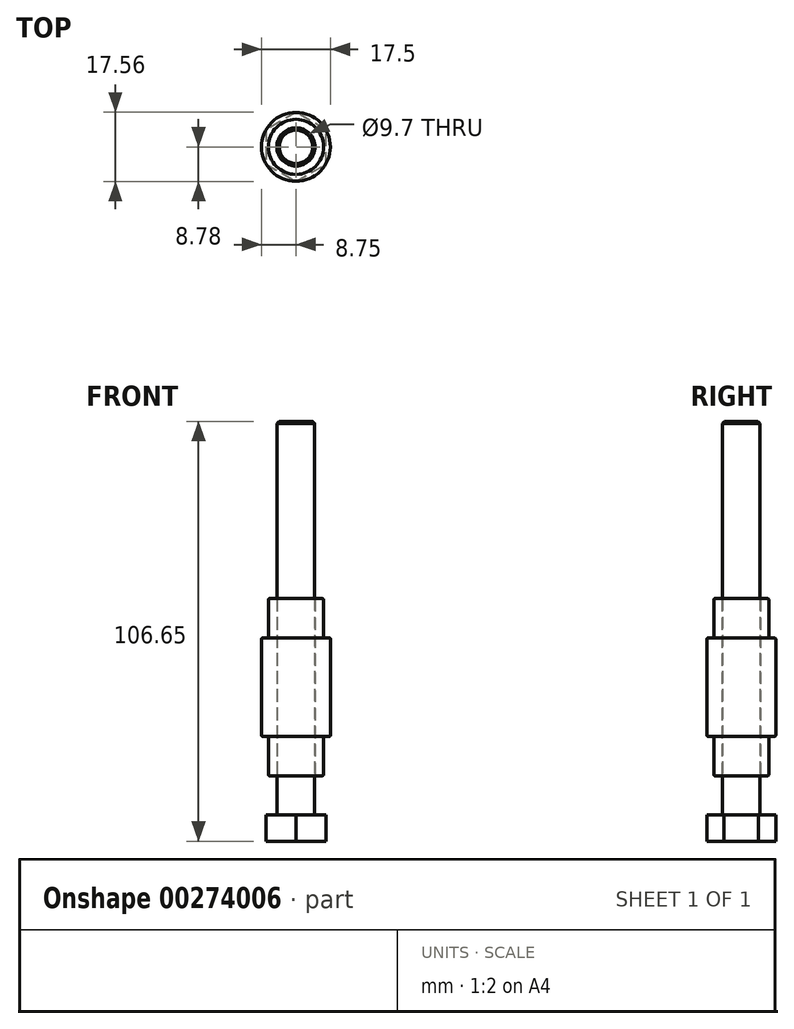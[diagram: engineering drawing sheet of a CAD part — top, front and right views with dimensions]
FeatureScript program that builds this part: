
annotation { "Feature Type Name" : "Feature", "Feature Type Description" : "" }
export const myFeature = defineFeature(function(context is Context, id is Id, definition is map)
    precondition{}
    {
        {
            var Q0;
            Q0=qCreatedBy(makeId("Top.planeOp"),FACE);
            var sketch = newSketch(context, id + "F0", { "sketchPlane" : qUnion([Q0])});
            skCircle(sketch, "E0", {"center": v(0, 0) * mm, "radius": 4.75 * mm});
            skSolve(sketch);
        }
        {
            var Q0;
            Q0=qSketchRegion(id+"F0",true);
            extrude(context, id + "F1", {"entities" : qUnion([Q0]), "depth" : 100 * mm});
        }
        {
            var Q0;
            Q0=makeQuery(id+"F1.opExtrude","CAP_FACE",FACE,{"disambiguationData":[OSD([sQuery(id+"F0.wireOp",EDGE,"E0")])],"isStart":true});
            var sketch = newSketch(context, id + "F2", { "sketchPlane" : qUnion([Q0])});
            skCircle(sketch, "E1.cCircle", {"center": v(0, 0) * mm, "radius": 7.6 * mm, "construction": true});
            skLineSegment(sketch, "E1.0", {"start": v(7.6, 4.39) * mm, "end": v(7.6, -4.39) * mm});
            skLineSegment(sketch, "E1.1", {"start": v(7.6, -4.39) * mm, "end": v(0, -8.78) * mm});
            skLineSegment(sketch, "E1.2", {"start": v(0, -8.78) * mm, "end": v(-7.6, -4.39) * mm});
            skLineSegment(sketch, "E1.3", {"start": v(-7.6, -4.39) * mm, "end": v(-7.6, 4.39) * mm});
            skLineSegment(sketch, "E1.4", {"start": v(-7.6, 4.39) * mm, "end": v(0, 8.78) * mm});
            skLineSegment(sketch, "E1.5", {"start": v(0, 8.78) * mm, "end": v(7.6, 4.39) * mm});
            skPoint(sketch, "E1.0.midPoint", {"position": v(7.6, 0) * mm});
            skSolve(sketch);
        }
        {
            var Q0;
            Q0=qSketchRegion(id+"F2",true);
            extrude(context, id + "F3", {"entities" : qUnion([Q0]), "operationType" : NewBodyOperationType.ADD, "depth" : (9.5 * 0.7) * mm});
        }
        {
            var Q0;
            Q0=makeQuery(id+"F1.opExtrude","CAP_EDGE",EDGE,{"disambiguationData":[OSD([sQuery(id+"F0.wireOp",EDGE,"E0")])],"isStart":false});
            var Q1;
            Q1=makeQuery(id+"F1.opExtrude","CAP_EDGE",EDGE,{"disambiguationData":[OSD([sQuery(id+"F0.wireOp",EDGE,"E0")])],"isStart":true});
            chamfer(context, id + "F4", {"entities" : qUnion([Q0, Q1]), "width" : 0.5 * mm, "tangentPropagation" : true});
        }
        {
            var Q0;
            Q0=qCreatedBy(makeId("Front.planeOp"),FACE);
            var sketch = newSketch(context, id + "F5", { "sketchPlane" : qUnion([Q0])});
            skLineSegment(sketch, "E2", {"start": v(0, 0) * mm, "end": v(0, 41.36) * mm, "construction": true});
            skLineSegment(sketch, "E3", {"start": v(4.85, 55) * mm, "end": v(4.85, 10) * mm});
            skLineSegment(sketch, "E4", {"start": v(4.85, 10) * mm, "end": v(7, 10) * mm});
            skLineSegment(sketch, "E5", {"start": v(7, 10) * mm, "end": v(7, 20) * mm});
            skLineSegment(sketch, "E6", {"start": v(7, 20) * mm, "end": v(8.75, 20) * mm});
            skLineSegment(sketch, "E7", {"start": v(8.75, 20) * mm, "end": v(8.75, 45) * mm});
            skLineSegment(sketch, "E8", {"start": v(8.75, 45) * mm, "end": v(7, 45) * mm});
            skLineSegment(sketch, "E9", {"start": v(7, 45) * mm, "end": v(7, 55) * mm});
            skLineSegment(sketch, "E10", {"start": v(7, 55) * mm, "end": v(4.85, 55) * mm});
            skSolve(sketch);
        }
        {
            var Q0;
            Q0=qSketchRegion(id+"F5",true);
            var Q1;
            Q1=sQuery(id+"F5.wireOp",EDGE,"E2");
            revolve(context, id + "F6", {"entities" : qUnion([Q0]), "axis" : qUnion([Q1]), "revolveType" : RevolveType.FULL});
        }
        {
            var Q0;
            Q0=makeQuery(id+"F6.opRevolve","SWEPT_EDGE",EDGE,{"disambiguationData":[OSD([sQuery(id+"F5.wireOp",EDGE,"E4"),sQuery(id+"F5.wireOp",EDGE,"E5")])]});
            var Q1;
            Q1=makeQuery(id+"F6.opRevolve","SWEPT_EDGE",EDGE,{"disambiguationData":[OSD([sQuery(id+"F5.wireOp",EDGE,"E5"),sQuery(id+"F5.wireOp",EDGE,"E6")])]});
            var Q2;
            Q2=makeQuery(id+"F6.opRevolve","SWEPT_EDGE",EDGE,{"disambiguationData":[OSD([sQuery(id+"F5.wireOp",EDGE,"E6"),sQuery(id+"F5.wireOp",EDGE,"E7")])]});
            var Q3;
            Q3=makeQuery(id+"F6.opRevolve","SWEPT_EDGE",EDGE,{"disambiguationData":[OSD([sQuery(id+"F5.wireOp",EDGE,"E7"),sQuery(id+"F5.wireOp",EDGE,"E8")])]});
            var Q4;
            Q4=makeQuery(id+"F6.opRevolve","SWEPT_EDGE",EDGE,{"disambiguationData":[OSD([sQuery(id+"F5.wireOp",EDGE,"E8"),sQuery(id+"F5.wireOp",EDGE,"E9")])]});
            var Q5;
            Q5=makeQuery(id+"F6.opRevolve","SWEPT_EDGE",EDGE,{"disambiguationData":[OSD([sQuery(id+"F5.wireOp",EDGE,"E9"),sQuery(id+"F5.wireOp",EDGE,"E10")])]});
            var Q6;
            Q6=makeQuery(id+"F6.opRevolve","SWEPT_EDGE",EDGE,{"disambiguationData":[OSD([sQuery(id+"F5.wireOp",EDGE,"E3"),sQuery(id+"F5.wireOp",EDGE,"E10")])]});
            var Q7;
            Q7=makeQuery(id+"F6.opRevolve","SWEPT_EDGE",EDGE,{"disambiguationData":[OSD([sQuery(id+"F5.wireOp",EDGE,"E3"),sQuery(id+"F5.wireOp",EDGE,"E4")])]});
            fillet(context, id + "F7", {"entities" : qUnion([Q0, Q1, Q2, Q3, Q4, Q5, Q6, Q7]), "radius" : 0.3 * mm, "tangentPropagation" : true, "allowEdgeOverflow" : false});
        }
    });
